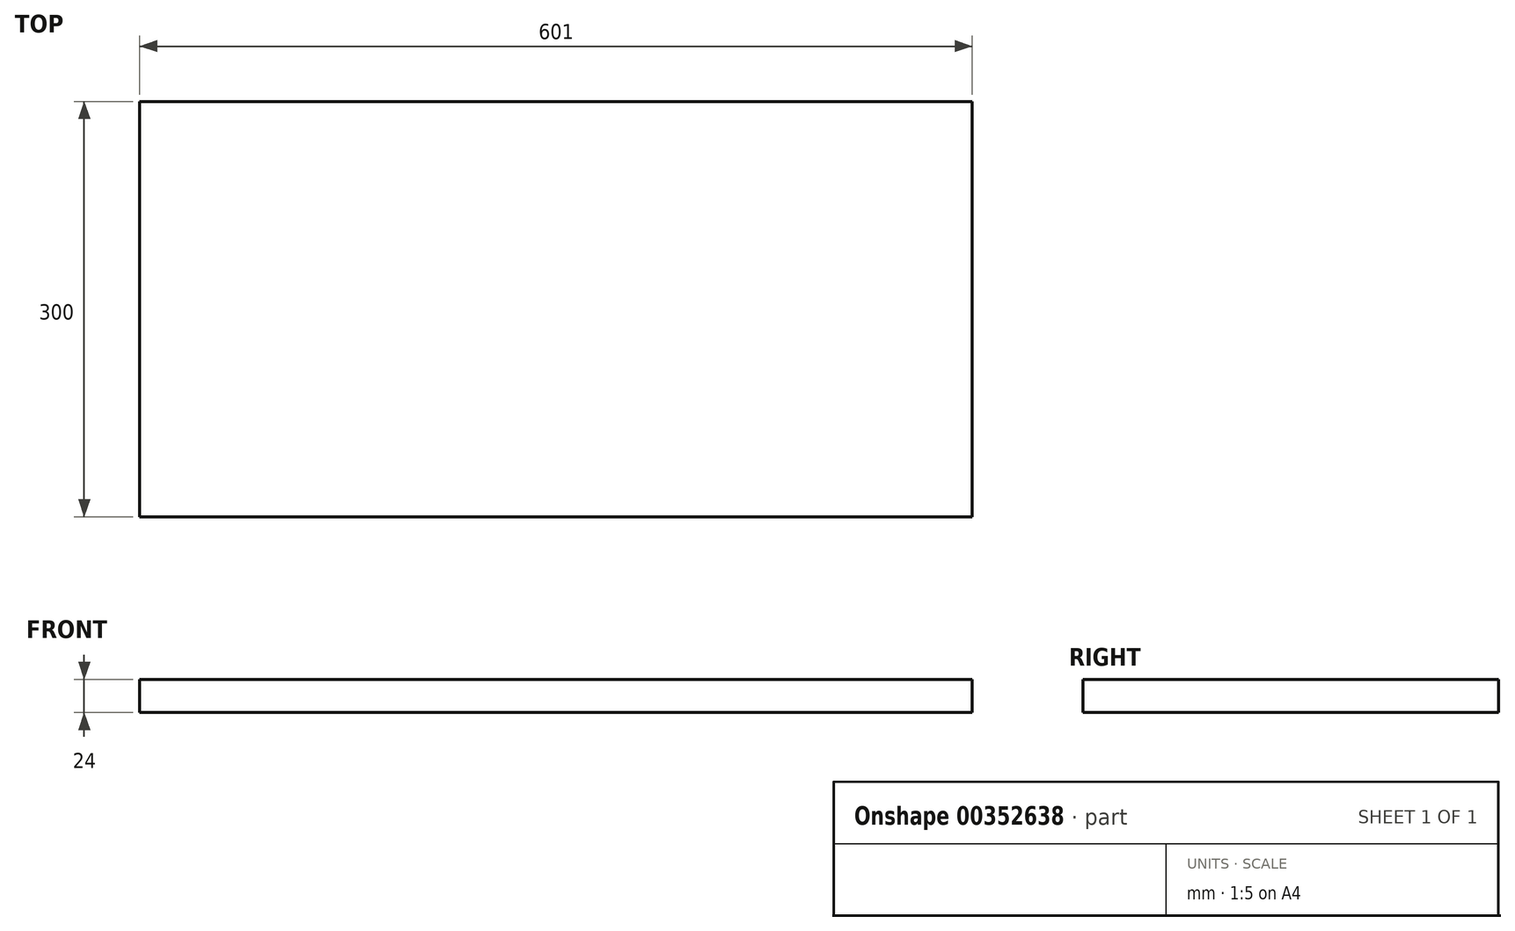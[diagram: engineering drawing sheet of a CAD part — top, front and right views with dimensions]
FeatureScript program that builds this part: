
annotation { "Feature Type Name" : "Feature", "Feature Type Description" : "" }
export const myFeature = defineFeature(function(context is Context, id is Id, definition is map)
    precondition{}
    {
        {
            var Q0;
            Q0=qCreatedBy(makeId("Front.planeOp"),FACE);
            var sketch = newSketch(context, id + "F0", { "sketchPlane" : qUnion([Q0])});
            skLineSegment(sketch, "E0", {"start": v(-24.18, 78.54) * mm, "end": v(0.82, 78.54) * mm});
            skLineSegment(sketch, "E1", {"start": v(-24.18, 78.54) * mm, "end": v(-312.18, 78.54) * mm});
            skLineSegment(sketch, "E2", {"start": v(-312.18, 78.54) * mm, "end": v(-312.18, 54.54) * mm});
            skLineSegment(sketch, "E3", {"start": v(-312.18, 54.54) * mm, "end": v(0.82, 54.54) * mm});
            skLineSegment(sketch, "E4", {"start": v(0.82, 54.54) * mm, "end": v(288.82, 54.54) * mm});
            skLineSegment(sketch, "E5", {"start": v(288.82, 54.54) * mm, "end": v(288.82, 78.54) * mm});
            skLineSegment(sketch, "E6", {"start": v(288.82, 78.54) * mm, "end": v(0.82, 78.54) * mm});
            skLineSegment(sketch, "E7", {"start": v(0.82, 78.54) * mm, "end": v(0.82, 54.54) * mm});
            skLineSegment(sketch, "E8", {"start": v(-24.18, 78.54) * mm, "end": v(-24.18, 54.54) * mm});
            skSolve(sketch);
        }
        {
            var Q0;
            Q0 = qSketchRegion(id + "F0", true);
            extrude(context, id + "F1", {"entities" : qUnion([Q0]), "depth" : 300 * mm, "offsetDistance" : 25 * mm});
        }
    });
